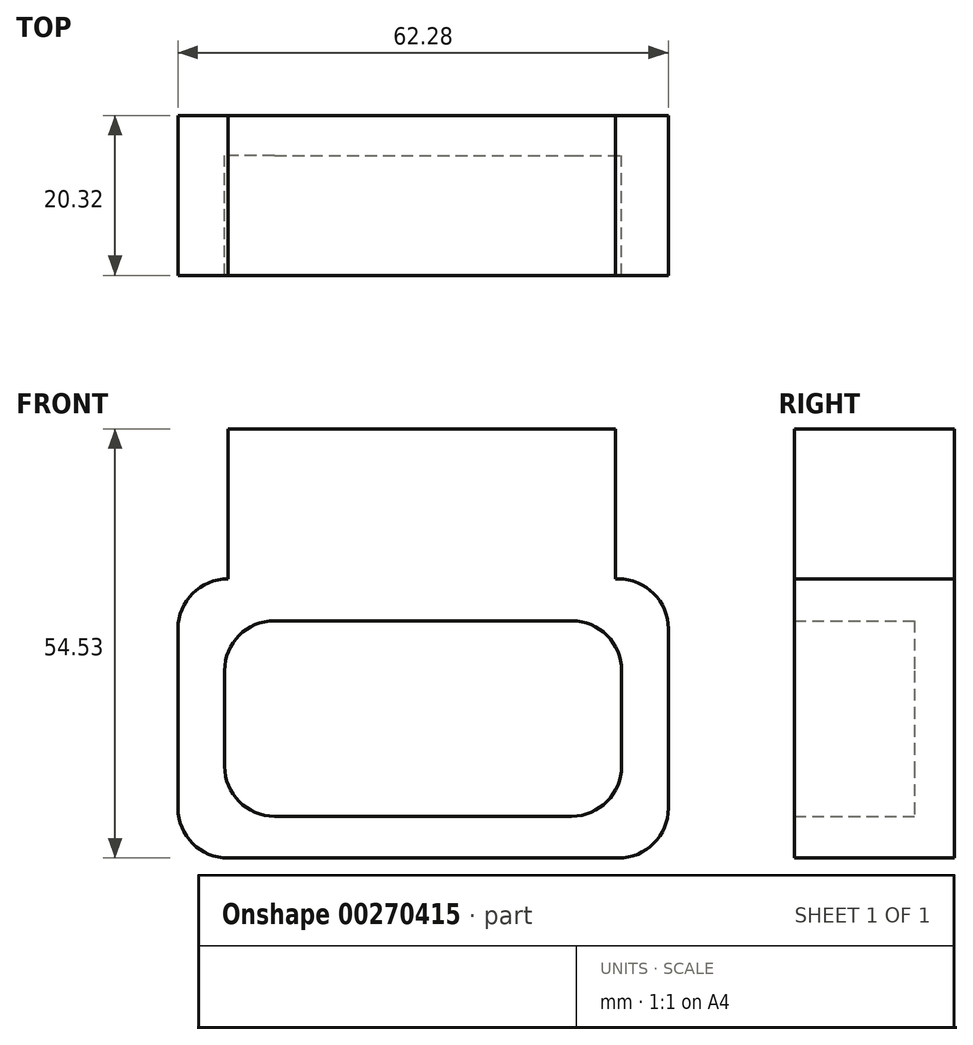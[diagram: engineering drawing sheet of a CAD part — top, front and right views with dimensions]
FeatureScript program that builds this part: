
annotation { "Feature Type Name" : "Feature", "Feature Type Description" : "" }
export const myFeature = defineFeature(function(context is Context, id is Id, definition is map)
    precondition{}
    {
        {
            var Q0;
            Q0=qCreatedBy(makeId("Front.planeOp"),FACE);
            var sketch = newSketch(context, id + "F0", { "sketchPlane" : qUnion([Q0])});
            skLineSegment(sketch, "E0.bottom", {"start": v(-18.87, 12.42) * mm, "end": v(18.87, 12.42) * mm});
            skLineSegment(sketch, "E0.top", {"start": v(-18.87, -12.42) * mm, "end": v(18.87, -12.42) * mm});
            skLineSegment(sketch, "E0.left", {"start": v(-25.22, 6.07) * mm, "end": v(-25.22, -6.07) * mm});
            skLineSegment(sketch, "E0.right", {"start": v(25.22, 6.07) * mm, "end": v(25.22, -6.07) * mm});
            skPoint(sketch, "E0.middle", {"position": v(0, 0) * mm});
            skPoint(sketch, "E1.visualSharp", {"position": v(-25.22, 12.42) * mm});
            skArc(sketch, "E1.filletArc", {"start": v(-18.87, 12.42) * mm, "mid": v(-23.36, 10.56) * mm, "end": v(-25.22, 6.07) * mm});
            skPoint(sketch, "E2.visualSharp", {"position": v(-25.22, -12.42) * mm});
            skArc(sketch, "E2.filletArc", {"start": v(-25.22, -6.07) * mm, "mid": v(-23.36, -10.56) * mm, "end": v(-18.87, -12.42) * mm});
            skPoint(sketch, "E3.visualSharp", {"position": v(25.22, 12.42) * mm});
            skArc(sketch, "E3.filletArc", {"start": v(25.22, 6.07) * mm, "mid": v(23.36, 10.56) * mm, "end": v(18.87, 12.42) * mm});
            skPoint(sketch, "E4.visualSharp", {"position": v(25.22, -12.42) * mm});
            skArc(sketch, "E4.filletArc", {"start": v(18.87, -12.42) * mm, "mid": v(23.36, -10.56) * mm, "end": v(25.22, -6.07) * mm});
            skLineSegment(sketch, "E5.bottom", {"start": v(-24.79, 17.74) * mm, "end": v(24.79, 17.74) * mm});
            skLineSegment(sketch, "E5.top", {"start": v(-24.79, -17.74) * mm, "end": v(24.79, -17.74) * mm});
            skLineSegment(sketch, "E5.left", {"start": v(-31.14, 11.39) * mm, "end": v(-31.14, -11.39) * mm});
            skLineSegment(sketch, "E5.right", {"start": v(31.14, 11.39) * mm, "end": v(31.14, -11.39) * mm});
            skPoint(sketch, "E6.visualSharp", {"position": v(-31.14, 17.74) * mm});
            skArc(sketch, "E6.filletArc", {"start": v(-24.79, 17.74) * mm, "mid": v(-29.28, 15.88) * mm, "end": v(-31.14, 11.39) * mm});
            skPoint(sketch, "E7.visualSharp", {"position": v(-31.14, -17.74) * mm});
            skArc(sketch, "E7.filletArc", {"start": v(-31.14, -11.39) * mm, "mid": v(-29.28, -15.88) * mm, "end": v(-24.79, -17.74) * mm});
            skPoint(sketch, "E8.visualSharp", {"position": v(31.14, 17.74) * mm});
            skArc(sketch, "E8.filletArc", {"start": v(31.14, 11.39) * mm, "mid": v(29.28, 15.88) * mm, "end": v(24.79, 17.74) * mm});
            skPoint(sketch, "E9.visualSharp", {"position": v(31.14, -17.74) * mm});
            skArc(sketch, "E9.filletArc", {"start": v(24.79, -17.74) * mm, "mid": v(29.28, -15.88) * mm, "end": v(31.14, -11.39) * mm});
            skLineSegment(sketch, "E10.bottom", {"start": v(-24.79, 17.74) * mm, "end": v(24.44, 17.74) * mm});
            skLineSegment(sketch, "E10.top", {"start": v(-24.79, 36.79) * mm, "end": v(24.44, 36.79) * mm});
            skLineSegment(sketch, "E10.left", {"start": v(-24.79, 17.74) * mm, "end": v(-24.79, 36.79) * mm});
            skLineSegment(sketch, "E10.right", {"start": v(24.44, 17.74) * mm, "end": v(24.44, 36.79) * mm});
            skSolve(sketch);
        }
        {
            var Q0;
            Q0=makeQuery(id+"F0.imprint","IMPRINT",FACE,{"disambiguationData":[TD([[makeQuery(id+"F0.imprint","IMPRINT",EDGE,{"derivedFrom":sQuery(id+"F0.wireOp",EDGE,"E0.bottom")}),1.0]])]});
            extrude(context, id + "F1", {"entities" : qUnion([Q0]), "depth" : 19.05 * mm});
        }
        {
            var Q0;
            Q0=makeQuery(id+"F0.imprint","IMPRINT",FACE,{"disambiguationData":[TD([[makeQuery(id+"F0.imprint","IMPRINT",EDGE,{"derivedFrom":sQuery(id+"F0.wireOp",EDGE,"E0.bottom")}),-1.0]])]});
            extrude(context, id + "F2", {"entities" : qUnion([Q0]), "operationType" : NewBodyOperationType.ADD, "depth" : 5.08 * mm});
        }
        {
            var Q0;
            Q0 = qSketchRegion(id + "F0", true);
            extrude(context, id + "F3", {"entities" : qUnion([Q0]), "operationType" : NewBodyOperationType.ADD, "depth" : 20.32 * mm});
        }
    });
